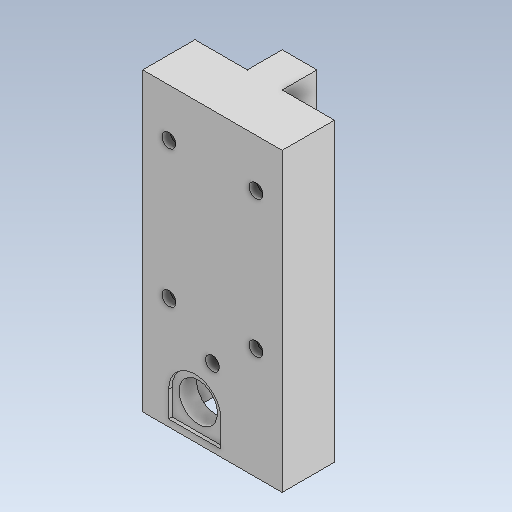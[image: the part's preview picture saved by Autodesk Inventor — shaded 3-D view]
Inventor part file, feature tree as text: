
AUTODESK INVENTOR PART (.ipt)
format: ipt  version: 2020 (Build 240168000, 168)  size: 283,136 bytes
history: native  units: mm
features: reference x19, sketch x17, extrude x15, projected_geometry x11, other x10, hole x2
ambient origin geometry x8: Origin, YZ Plane, XZ Plane, XY Plane, X Axis, Y Axis, Z Axis, Center Point
bodies: Body1 (feature_tree)
feature tree (74):
  other  "솔리드1"
  extrude  "돌출1"  Depth=20.0mm TaperAngle=0.0deg
  extrude  "돌출2"  Depth=25.3mm TaperAngle=0.0deg
  extrude  "돌출3"  Depth=137.5mm
  extrude  "돌출4"  Depth=40.0mm TaperAngle=0.0deg
  extrude  "돌출5"  Depth=30.0mm TaperAngle=0.0deg
  extrude  "돌출6"  Depth=10.0mm
  extrude  "돌출7"  Depth=15.0mm
  extrude  "돌출8"  Depth=5.0mm TaperAngle=0.0deg
  extrude  "돌출9"  Depth=32.0mm
  hole  "구멍1"  [1 undecoded]
  extrude  "돌출10"  Depth=17.0mm
  extrude  "돌출11"  Depth=30.0mm TaperAngle=0.0deg
  hole  "구멍2"  [1 undecoded]
  extrude  "돌출16"  Depth=12.0mm TaperAngle=0.0deg
  extrude  "돌출18"  Depth=30.0mm
  extrude  "돌출19"  Depth=2.0mm TaperAngle=0.0deg
  extrude  "돌출20"  Depth=60.0mm
  sketch  "스케치1"
  reference  "참조1"
  reference  "참조2"
  reference  "참조3"
  reference  "참조4"
  reference  "참조5"
  reference  "참조6"
  reference  "참조7"
  reference  "참조8"
  sketch  "스케치2"
  reference  "참조9"
  reference  "참조10"
  reference  "참조11"
  sketch  "스케치3"
  reference  "참조12"
  reference  "참조13"
  sketch  "스케치4"
  reference  "참조14"
  reference  "참조15"
  reference  "참조16"
  reference  "참조17"
  sketch  "스케치6"
  projected_geometry  "투영된 루프1"
  sketch  "스케치7"
  projected_geometry  "투영된 루프2"
  projected_geometry  "투영된 루프3"
  sketch  "스케치8"
  projected_geometry  "투영된 루프4"
  sketch  "스케치9"
  projected_geometry  "투영된 루프5"
  sketch  "스케치10"
  projected_geometry  "투영된 루프6"
  sketch  "스케치11"
  reference  "참조18"
  reference  "참조19"
  sketch  "스케치12"
  projected_geometry  "투영된 루프7"
  sketch  "스케치13"
  sketch  "스케치14"
  sketch  "스케치19"
  projected_geometry  "투영된 루프12"
  sketch  "스케치21"
  projected_geometry  "투영된 루프14"
  sketch  "스케치22"
  projected_geometry  "투영된 루프15"
  sketch  "스케치23"
  projected_geometry  "투영된 루프16"
  parser-record x2  (decoder bookkeeping rows leaked as tree rows — omitted from the tree; the rows remain in map.json)
  other  "v6.iam"
  other  "AL_profile_final:1"
  other  "AL_profile_final:2"
  other  "cross_AL_profile:2"
  other  "caster_wheel_mount:1"
  other  "cross_AL_profile:1"
  other  "Axel_arch_final_v4:2"
note: 2 required parameter values undecoded (feature->parameter linkage not recoverable at this tier; creation-order binding heuristic only, values carry confidence <= 0.55)
note: 2 file-system paths scrubbed to <path> (originals preserved in map.json)
